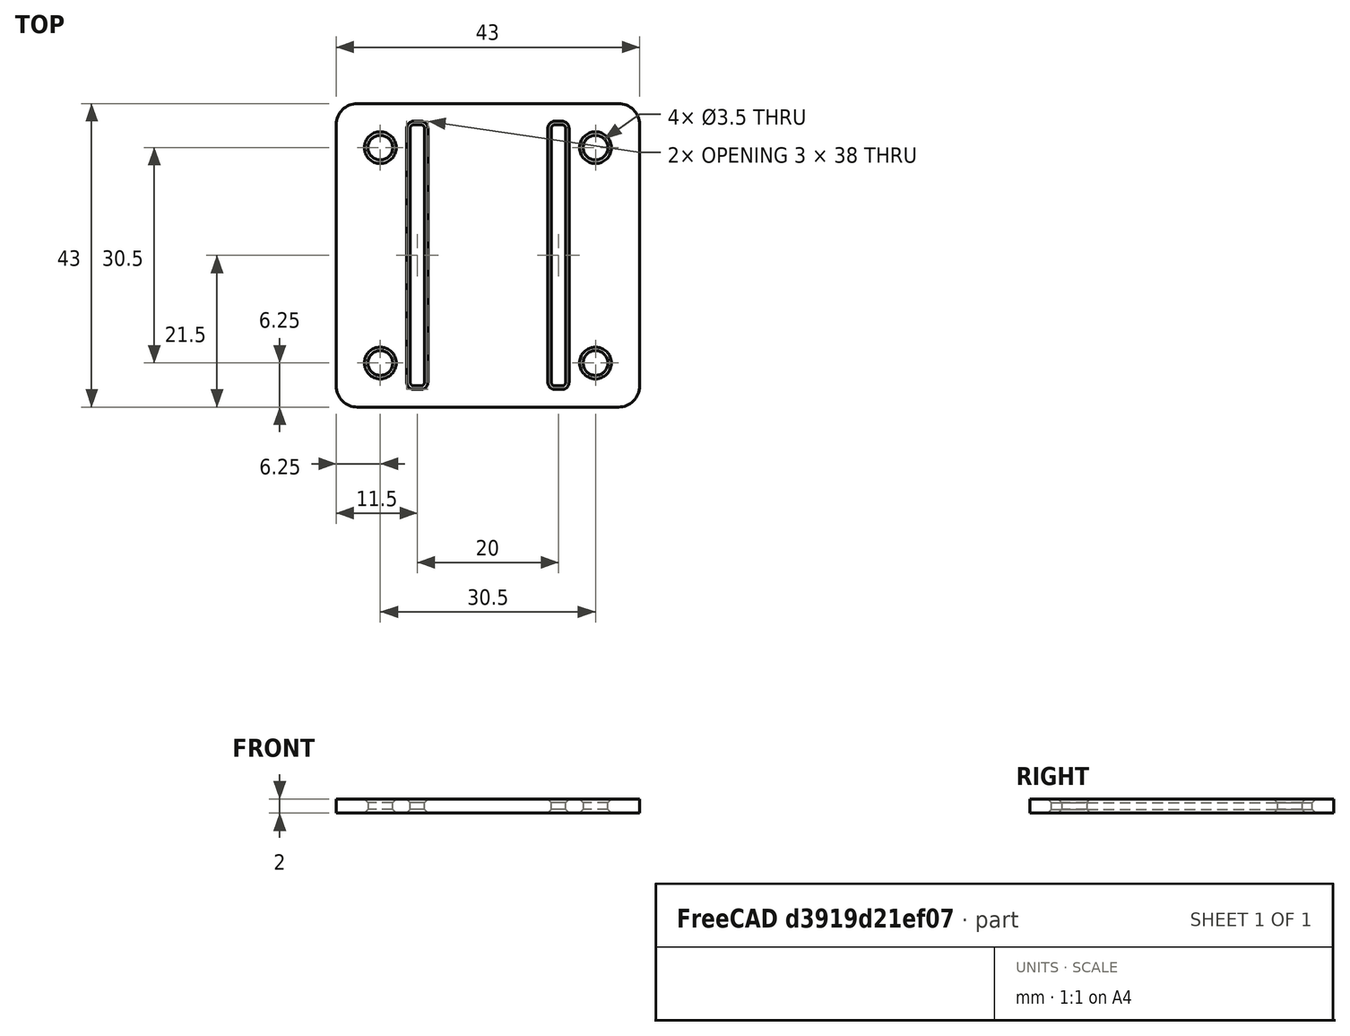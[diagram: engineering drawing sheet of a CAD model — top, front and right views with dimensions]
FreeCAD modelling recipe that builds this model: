
FCSTD DOCUMENT  (FreeCAD 0.18.1R)
Label: plate_ardu_rec
License: All rights reserved
LicenseURL: http://en.wikipedia.org/wiki/All_rights_reserved
objects: Part::Cut×6, Part::Part2DObjectPython×5, Part::Extrusion×5, Part::Box×2, Part::Fillet×2, Part::Chamfer×2
note: 22 computed .brp shape members not serialized (recipe doc carries the construction recipe); baked Part::Feature solids carry a one-line shape summary decoded from their .brp

FEATURE [Part::Part2DObjectPython] Circle  label="Circle3"  # Draft 2D object (typed FeaturePython)
  FirstAngle = 0
  LastAngle = 0
  MakeFace = false
  Placement = pos=(36.75,6.25,0) rot=(0,0,1;0rad)
  Radius = 1.75
FEATURE [Part::Part2DObjectPython] Circle001  label="Circle2"  # Draft 2D object (typed FeaturePython)
  FirstAngle = 0
  LastAngle = 0
  MakeFace = false
  Placement = pos=(36.75,36.75,0) rot=(0,0,1;0rad)
  Radius = 1.75
FEATURE [Part::Part2DObjectPython] Circle002  label="Circle0"  # Draft 2D object (typed FeaturePython)
  FirstAngle = 0
  LastAngle = 0
  MakeFace = false
  Placement = pos=(6.25,6.25,0) rot=(0,0,1;0rad)
  Radius = 1.75
FEATURE [Part::Part2DObjectPython] Circle003  label="Circle1"  # Draft 2D object (typed FeaturePython)
  FirstAngle = 0
  LastAngle = 0
  MakeFace = false
  Placement = pos=(6.25,36.75,0) rot=(0,0,1;0rad)
  Radius = 1.75
FEATURE [Part::Part2DObjectPython] Rectangle  # Draft 2D object (typed FeaturePython)
  ChamferSize = 0
  Columns = 1
  FilletRadius = 0
  Height = 43
  Length = 43
  MakeFace = false
  Rows = 1
FEATURE [Part::Extrusion] Extrude
  Base = -> Circle
  Dir = (0,0,1)
  DirMode = 2
  FaceMakerClass = Part::FaceMakerBullseye
  LengthFwd = 2
  LengthRev = 0
  Solid = true
  Symmetric = false
FEATURE [Part::Extrusion] Extrude001
  Base = -> Circle001
  Dir = (0,0,1)
  DirMode = 2
  FaceMakerClass = Part::FaceMakerBullseye
  LengthFwd = 2
  LengthRev = 0
  Solid = true
  Symmetric = false
FEATURE [Part::Extrusion] Extrude002
  Base = -> Circle002
  Dir = (0,0,1)
  DirMode = 2
  FaceMakerClass = Part::FaceMakerBullseye
  LengthFwd = 2
  LengthRev = 0
  Solid = true
  Symmetric = false
FEATURE [Part::Extrusion] Extrude003
  Base = -> Circle003
  Dir = (0,0,1)
  DirMode = 2
  FaceMakerClass = Part::FaceMakerBullseye
  LengthFwd = 2
  LengthRev = 0
  Solid = true
  Symmetric = false
FEATURE [Part::Extrusion] Extrude004
  Base = -> Rectangle
  Dir = (0,0,1)
  DirMode = 2
  FaceMakerClass = Part::FaceMakerBullseye
  LengthFwd = 2
  LengthRev = 0
  Solid = true
  Symmetric = false
FEATURE [Part::Cut] Cut
  Base = -> Extrude004
  Tool = -> Extrude003
FEATURE [Part::Cut] Cut001
  Base = -> Cut
  Tool = -> Extrude002
FEATURE [Part::Cut] Cut002
  Base = -> Cut001
  Tool = -> Extrude001
FEATURE [Part::Cut] Cut003
  Base = -> Cut002
  Tool = -> Extrude
FEATURE [Part::Box] Box  label="Cube"
  AttacherType = Attacher::AttachEngine3D
  Height = 2
  Length = 2
  Placement = pos=(10.5,3,0) rot=(0,0,1;0rad)
  Width = 37
FEATURE [Part::Box] Box001  label="Cube001"
  AttacherType = Attacher::AttachEngine3D
  Height = 2
  Length = 2
  Placement = pos=(30.5,3,0) rot=(0,0,1;0rad)
  Width = 37
FEATURE [Part::Cut] Cut004
  Base = -> Cut003
  Tool = -> Box
FEATURE [Part::Cut] Cut005
  Base = -> Cut004
  Tool = -> Box001
FEATURE [Part::Fillet] Fillet
  Base = -> Cut005
  Edges = 4 edges r=3: [Edge1,Edge2,Edge5,Edge8]
FEATURE [Part::Fillet] Fillet001
  Base = -> Fillet
  Edges = 8 edges r=0.5: [Edge49,Edge50,Edge51,Edge52,Edge53,Edge54,Edge55,Edge56]
FEATURE [Part::Chamfer] Chamfer
  Base = -> Fillet001
  Edges = 20 edges r=0.5: [Edge29,Edge33,Edge35,Edge37,Edge39,Edge41,Edge43,Edge44,Edge62,Edge64,Edge66,Edge68,Edge69,Edge73,Edge75,Edge77,Edge79,Edge81,Edge83,Edge84]
FEATURE [Part::Chamfer] Chamfer001
  Base = -> Chamfer
  Edges = 20 edges r=0.5: [Edge3,Edge6,Edge11,Edge12,Edge13,Edge14,Edge15,Edge16,Edge25,Edge26,Edge27,Edge28,Edge29,Edge30,Edge31,Edge32,Edge33,Edge34,Edge35,Edge36]
